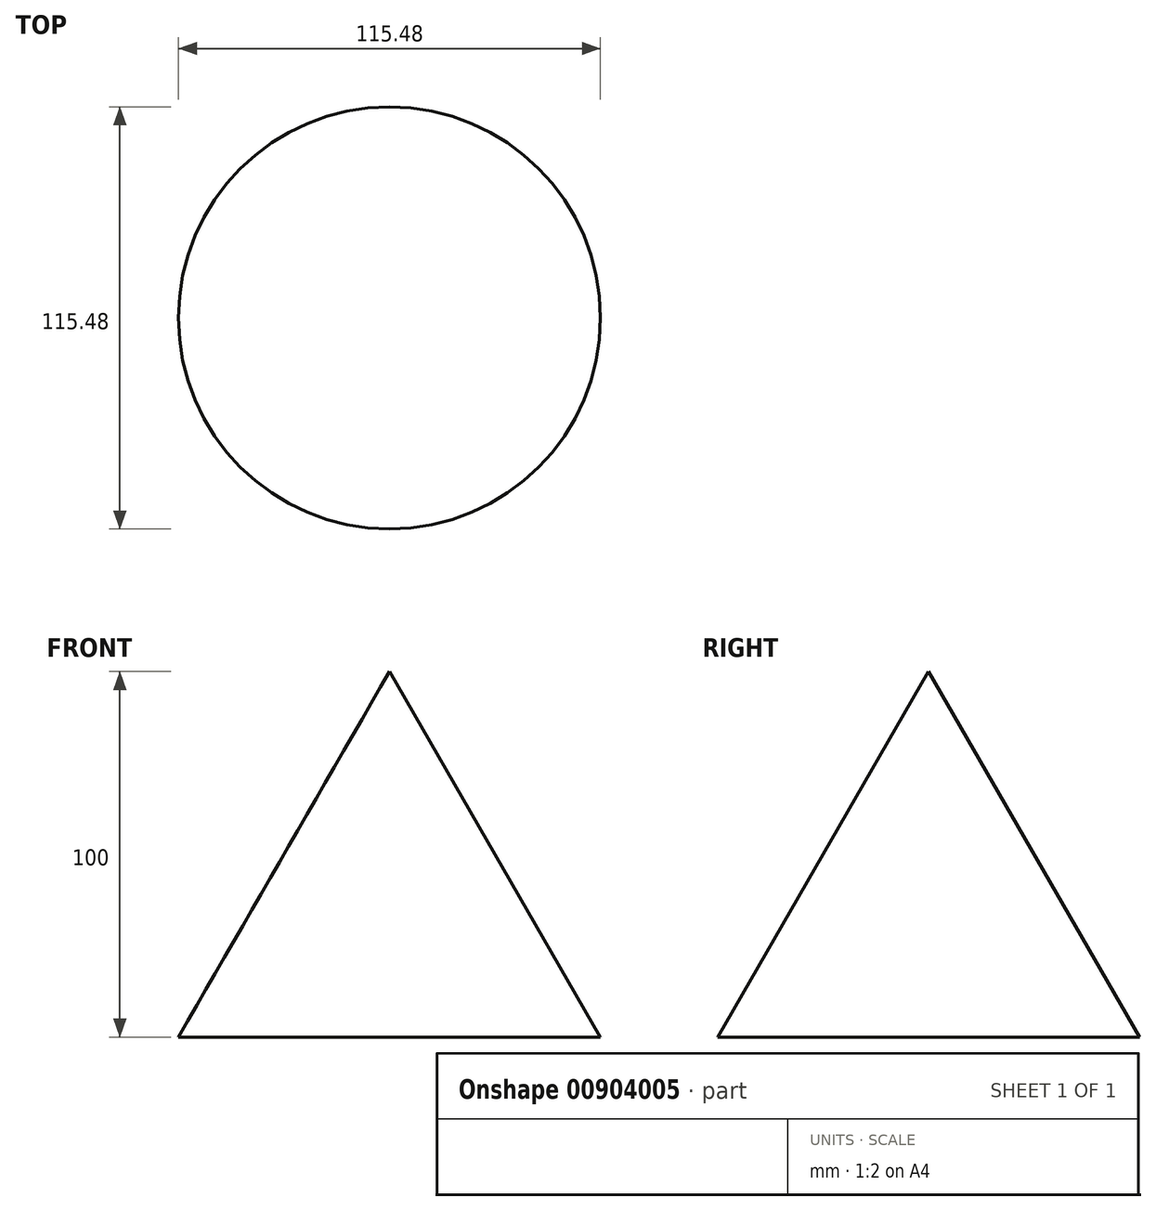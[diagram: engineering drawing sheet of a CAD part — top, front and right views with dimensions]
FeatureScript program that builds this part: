
annotation { "Feature Type Name" : "Feature", "Feature Type Description" : "" }
export const myFeature = defineFeature(function(context is Context, id is Id, definition is map)
    precondition{}
    {
        {
            var Q0;
            Q0=qCreatedBy(makeId("Front.planeOp"),FACE);
            var sketch = newSketch(context, id + "F0", { "sketchPlane" : qUnion([Q0])});
            skLineSegment(sketch, "E0", {"start": v(0, 100) * mm, "end": v(0, 0) * mm});
            skLineSegment(sketch, "E1", {"start": v(0, 0) * mm, "end": v(57.74, 0) * mm});
            skLineSegment(sketch, "E2", {"start": v(57.74, 0) * mm, "end": v(0, 100) * mm});
            skSolve(sketch);
        }
        {
            var Q0;
            Q0 = qSketchRegion(id + "F0", true);
            var Q1;
            Q1=sQuery(id+"F0.wireOp",EDGE,"E0");
            revolve(context, id + "F1", {"surfaceOperationType" : NewSurfaceOperationType.NEW, "entities" : qUnion([Q0]), "axis" : qUnion([Q1]), "revolveType" : RevolveType.FULL});
        }
    });
